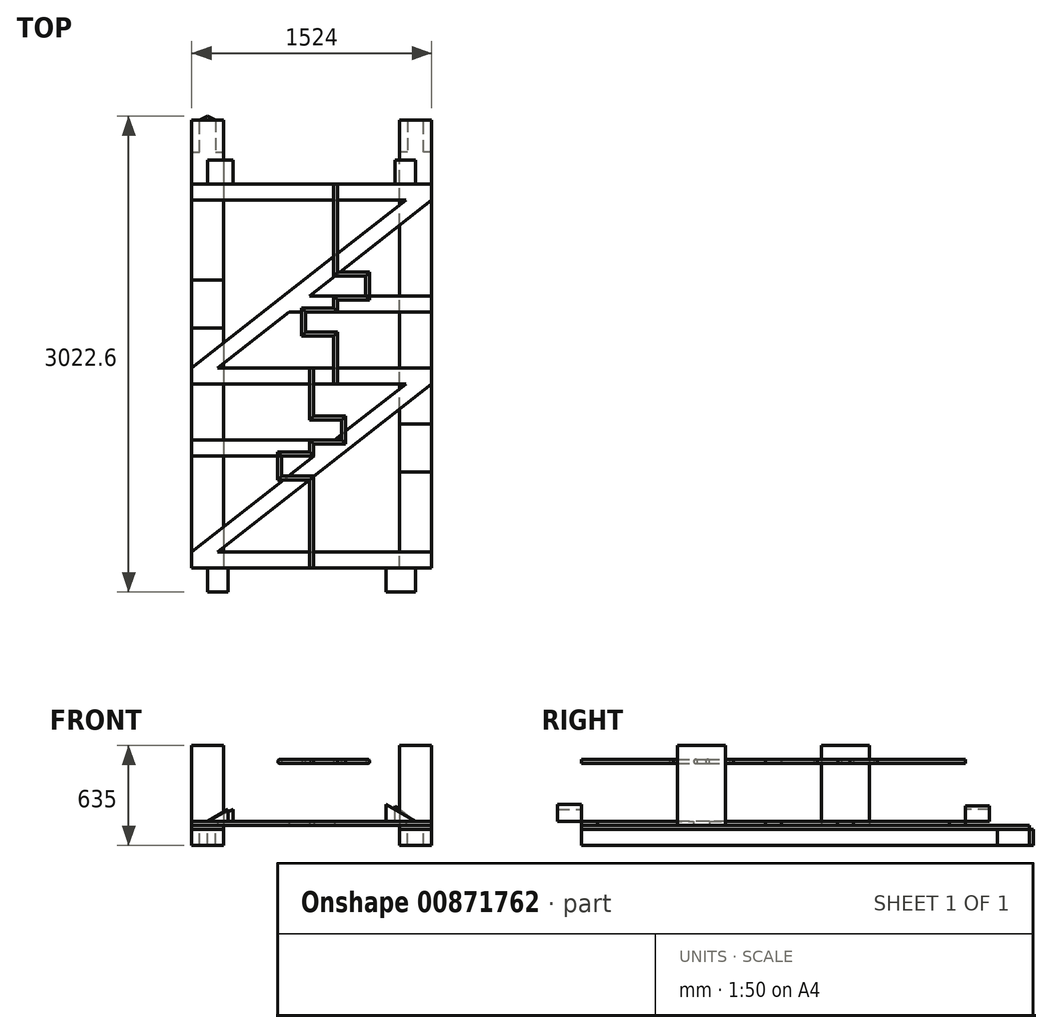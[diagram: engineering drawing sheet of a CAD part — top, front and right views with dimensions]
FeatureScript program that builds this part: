
annotation { "Feature Type Name" : "Feature", "Feature Type Description" : "" }
export const myFeature = defineFeature(function(context is Context, id is Id, definition is map)
    precondition{}
    {
        {
            var Q0;
            Q0=qCreatedBy(makeId("Top.planeOp"),FACE);
            cPlane(context, id + "F0", {"entities" : qUnion([Q0]), "cplaneType" : CPlaneType.OFFSET, "offset" : 406.4 * mm, "width" : 152.4 * mm, "height" : 152.4 * mm});
        }
        {
            var Q0;
            Q0=qCreatedBy(makeId("Top.planeOp"),FACE);
            var sketch = newSketch(context, id + "F1", { "sketchPlane" : qUnion([Q0])});
            skLineSegment(sketch, "E0.bottom", {"start": v(-762, 1219.2) * mm, "end": v(-558.8, 1219.2) * mm});
            skLineSegment(sketch, "E0.top", {"start": v(-762, -1219.2) * mm, "end": v(-558.8, -1219.2) * mm});
            skLineSegment(sketch, "E0.left", {"start": v(-762, 1219.2) * mm, "end": v(-762, -1219.2) * mm});
            skLineSegment(sketch, "E0.right", {"start": v(-558.8, 1219.2) * mm, "end": v(-558.8, -1219.2) * mm});
            skLineSegment(sketch, "E1.bottom", {"start": v(-558.8, -1219.2) * mm, "end": v(558.8, -1219.2) * mm});
            skLineSegment(sketch, "E1.top", {"start": v(-558.8, 1219.2) * mm, "end": v(558.8, 1219.2) * mm});
            skLineSegment(sketch, "E1.right", {"start": v(558.8, -1219.2) * mm, "end": v(558.8, 1219.2) * mm});
            skLineSegment(sketch, "E2.bottom", {"start": v(558.8, -1219.2) * mm, "end": v(762, -1219.2) * mm});
            skLineSegment(sketch, "E2.top", {"start": v(558.8, 1219.2) * mm, "end": v(762, 1219.2) * mm});
            skLineSegment(sketch, "E2.right", {"start": v(762, -1219.2) * mm, "end": v(762, 1219.2) * mm});
            skLineSegment(sketch, "E3", {"start": v(0, 1219.2) * mm, "end": v(0, -1219.2) * mm});
            skLineSegment(sketch, "E4", {"start": v(152.4, 1219.2) * mm, "end": v(152.4, -50.8) * mm});
            skPoint(sketch, "E5", {"position": v(0, 0) * mm});
            skLineSegment(sketch, "E6", {"start": v(152.4, 647.7) * mm, "end": v(355.6, 647.7) * mm});
            skLineSegment(sketch, "E7", {"start": v(355.6, 647.7) * mm, "end": v(355.6, 495.3) * mm});
            skLineSegment(sketch, "E8", {"start": v(355.6, 495.3) * mm, "end": v(152.4, 495.3) * mm});
            skPoint(sketch, "E9", {"position": v(152.4, 457.2) * mm});
            skPoint(sketch, "E10", {"position": v(355.6, 571.5) * mm});
            skLineSegment(sketch, "E11", {"start": v(152.4, 419.1) * mm, "end": v(-50.8, 419.1) * mm});
            skLineSegment(sketch, "E12", {"start": v(-50.8, 419.1) * mm, "end": v(-50.8, 266.7) * mm});
            skLineSegment(sketch, "E13", {"start": v(-50.8, 266.7) * mm, "end": v(152.4, 266.7) * mm});
            skPoint(sketch, "E14", {"position": v(-50.8, 342.9) * mm});
            skLineSegment(sketch, "E15", {"start": v(-762, 609.6) * mm, "end": v(-558.8, 609.6) * mm});
            skLineSegment(sketch, "E16", {"start": v(-762, 304.8) * mm, "end": v(-558.8, 304.8) * mm});
            skPoint(sketch, "E17", {"position": v(-558.8, 457.2) * mm});
            skLineSegment(sketch, "E18", {"start": v(762, -304.8) * mm, "end": v(558.8, -304.8) * mm});
            skLineSegment(sketch, "E19", {"start": v(558.8, -304.8) * mm, "end": v(558.8, -609.6) * mm});
            skLineSegment(sketch, "E20", {"start": v(558.8, -609.6) * mm, "end": v(762, -609.6) * mm});
            skPoint(sketch, "E21", {"position": v(558.8, -457.2) * mm});
            skLineSegment(sketch, "E22", {"start": v(-762, 1219.2) * mm, "end": v(-762, 1422.4) * mm});
            skLineSegment(sketch, "E23", {"start": v(-762, 1422.4) * mm, "end": v(-558.8, 1422.4) * mm});
            skLineSegment(sketch, "E24", {"start": v(-558.8, 1422.4) * mm, "end": v(-558.8, 1219.2) * mm});
            skLineSegment(sketch, "E25", {"start": v(-660.4, 1422.4) * mm, "end": v(-660.4, 1219.2) * mm});
            skLineSegment(sketch, "E26", {"start": v(-711.2, 1422.4) * mm, "end": v(-711.2, 1625.6) * mm});
            skLineSegment(sketch, "E27", {"start": v(-711.2, 1625.6) * mm, "end": v(-609.6, 1625.6) * mm});
            skLineSegment(sketch, "E28", {"start": v(-609.6, 1625.6) * mm, "end": v(-609.6, 1422.4) * mm});
            skLineSegment(sketch, "E29", {"start": v(-711.2, 1625.6) * mm, "end": v(-660.4, 1651) * mm});
            skLineSegment(sketch, "E30", {"start": v(-660.4, 1651) * mm, "end": v(-609.6, 1625.6) * mm});
            skLineSegment(sketch, "E31", {"start": v(-660.4, 1625.6) * mm, "end": v(-660.4, 1651) * mm, "construction": true});
            skLineSegment(sketch, "E32.MirrorCS", {"start": v(711.2, 1625.6) * mm, "end": v(609.6, 1625.6) * mm});
            skLineSegment(sketch, "E33.MirrorCS", {"start": v(660.4, 1625.6) * mm, "end": v(660.4, 1651) * mm, "construction": true});
            skLineSegment(sketch, "E34.MirrorCS", {"start": v(660.4, 1651) * mm, "end": v(609.6, 1625.6) * mm});
            skLineSegment(sketch, "E35.MirrorCS", {"start": v(711.2, 1625.6) * mm, "end": v(660.4, 1651) * mm});
            skLineSegment(sketch, "E36.MirrorCS", {"start": v(762, 1422.4) * mm, "end": v(558.8, 1422.4) * mm});
            skLineSegment(sketch, "E37.MirrorCS", {"start": v(609.6, 1625.6) * mm, "end": v(609.6, 1422.4) * mm});
            skLineSegment(sketch, "E38.MirrorCS", {"start": v(711.2, 1422.4) * mm, "end": v(711.2, 1625.6) * mm});
            skLineSegment(sketch, "E39.MirrorCS", {"start": v(558.8, 1422.4) * mm, "end": v(558.8, 1219.2) * mm});
            skLineSegment(sketch, "E40.MirrorCS", {"start": v(762, 1219.2) * mm, "end": v(762, 1422.4) * mm});
            skLineSegment(sketch, "E41.MirrorCS", {"start": v(660.4, 1422.4) * mm, "end": v(660.4, 1219.2) * mm});
            skLineSegment(sketch, "E42", {"start": v(-762, 1422.4) * mm, "end": v(-762, 1625.6) * mm});
            skLineSegment(sketch, "E43", {"start": v(-762, 1625.6) * mm, "end": v(-558.8, 1625.6) * mm});
            skLineSegment(sketch, "E44", {"start": v(-558.8, 1625.6) * mm, "end": v(-558.8, 1422.4) * mm});
            skLineSegment(sketch, "E45.MirrorCS", {"start": v(558.8, 1625.6) * mm, "end": v(558.8, 1422.4) * mm});
            skLineSegment(sketch, "E46.MirrorCS", {"start": v(762, 1422.4) * mm, "end": v(762, 1625.6) * mm});
            skLineSegment(sketch, "E47.MirrorCS", {"start": v(762, 1625.6) * mm, "end": v(558.8, 1625.6) * mm});
            skLineSegment(sketch, "E48", {"start": v(-660.4, -1219.2) * mm, "end": v(-660.4, 1219.2) * mm, "construction": true});
            skLineSegment(sketch, "E49", {"start": v(660.4, -1219.2) * mm, "end": v(660.4, 1219.2) * mm, "construction": true});
            skSolve(sketch);
        }
        {
            var Q0;
            {var subQ3=sQuery(id+"F1.wireOp",EDGE,"E15");Q0=makeQuery(id+"F1.imprint","IMPRINT",FACE,{"disambiguationData":[TD([[makeQuery(id+"F1.imprint","IMPRINT",EDGE,{"derivedFrom":subQ3}),1.0]])]});}
            var Q1;
            {var subQ0=sQuery(id+"F1.wireOp",EDGE,"E15");Q1=makeQuery(id+"F1.imprint","IMPRINT",FACE,{"disambiguationData":[TD([[makeQuery(id+"F1.imprint","IMPRINT",EDGE,{"derivedFrom":subQ0}),-1.0]])]});}
            var Q2;
            {var subQ0=sQuery(id+"F1.wireOp",EDGE,"E0.top");Q2=makeQuery(id+"F1.imprint","IMPRINT",FACE,{"disambiguationData":[TD([[makeQuery(id+"F1.imprint","IMPRINT",EDGE,{"derivedFrom":subQ0}),1.0]])]});}
            var Q3;
            {var subQ0=sQuery(id+"F1.wireOp",EDGE,"E2.bottom");Q3=makeQuery(id+"F1.imprint","IMPRINT",FACE,{"disambiguationData":[TD([[makeQuery(id+"F1.imprint","IMPRINT",EDGE,{"derivedFrom":subQ0}),1.0]])]});}
            var Q4;
            {var subQ3=sQuery(id+"F1.wireOp",EDGE,"E18");Q4=makeQuery(id+"F1.imprint","IMPRINT",FACE,{"disambiguationData":[TD([[makeQuery(id+"F1.imprint","IMPRINT",EDGE,{"derivedFrom":subQ3}),-1.0]])]});}
            var Q5;
            {var subQ0=sQuery(id+"F1.wireOp",EDGE,"E18");Q5=makeQuery(id+"F1.imprint","IMPRINT",FACE,{"disambiguationData":[TD([[makeQuery(id+"F1.imprint","IMPRINT",EDGE,{"derivedFrom":subQ0}),1.0]])]});}
            var Q6;
            {var subQ1=sQuery(id+"F1.wireOp",EDGE,"E26");Q6=makeQuery(id+"F1.imprint","IMPRINT",FACE,{"disambiguationData":[TD([[makeQuery(id+"F1.imprint","IMPRINT",EDGE,{"derivedFrom":subQ1}),-1.0]])]});}
            var Q7;
            {var subQ0=sQuery(id+"F1.wireOp",EDGE,"E29");Q7=makeQuery(id+"F1.imprint","IMPRINT",FACE,{"disambiguationData":[TD([[makeQuery(id+"F1.imprint","IMPRINT",EDGE,{"derivedFrom":subQ0}),-1.0]])]});}
            var Q8;
            {var subQ0=sQuery(id+"F1.wireOp",EDGE,"E30");Q8=makeQuery(id+"F1.imprint","IMPRINT",FACE,{"disambiguationData":[TD([[makeQuery(id+"F1.imprint","IMPRINT",EDGE,{"derivedFrom":subQ0}),-1.0]])]});}
            var Q9;
            {var subQ0=sQuery(id+"F1.wireOp",EDGE,"E24");Q9=makeQuery(id+"F1.imprint","IMPRINT",FACE,{"disambiguationData":[TD([[makeQuery(id+"F1.imprint","IMPRINT",EDGE,{"derivedFrom":subQ0}),-1.0]])]});}
            var Q10;
            {var subQ3=sQuery(id+"F1.wireOp",EDGE,"E22");Q10=makeQuery(id+"F1.imprint","IMPRINT",FACE,{"disambiguationData":[TD([[makeQuery(id+"F1.imprint","IMPRINT",EDGE,{"derivedFrom":subQ3}),-1.0]])]});}
            var Q11;
            {var subQ0=sQuery(id+"F1.wireOp",EDGE,"E40.MirrorCS");Q11=makeQuery(id+"F1.imprint","IMPRINT",FACE,{"disambiguationData":[TD([[makeQuery(id+"F1.imprint","IMPRINT",EDGE,{"derivedFrom":subQ0}),1.0]])]});}
            var Q12;
            {var subQ0=sQuery(id+"F1.wireOp",EDGE,"E37.MirrorCS");Q12=makeQuery(id+"F1.imprint","IMPRINT",FACE,{"disambiguationData":[TD([[makeQuery(id+"F1.imprint","IMPRINT",EDGE,{"derivedFrom":subQ0}),1.0]])]});}
            var Q13;
            {var subQ0=sQuery(id+"F1.wireOp",EDGE,"E39.MirrorCS");Q13=makeQuery(id+"F1.imprint","IMPRINT",FACE,{"disambiguationData":[TD([[makeQuery(id+"F1.imprint","IMPRINT",EDGE,{"derivedFrom":subQ0}),1.0]])]});}
            var Q14;
            {var subQ2=sQuery(id+"F1.wireOp",EDGE,"E33.MirrorCS");Q14=makeQuery(id+"F1.imprint","IMPRINT",FACE,{"disambiguationData":[TD([[makeQuery(id+"F1.imprint","IMPRINT",EDGE,{"derivedFrom":subQ2}),1.0]])]});}
            var Q15;
            {var subQ2=sQuery(id+"F1.wireOp",EDGE,"E33.MirrorCS");Q15=makeQuery(id+"F1.imprint","IMPRINT",FACE,{"disambiguationData":[TD([[makeQuery(id+"F1.imprint","IMPRINT",EDGE,{"derivedFrom":subQ2}),-1.0]])]});}
            extrude(context, id + "F2", {"entities" : qUnion([Q0, Q1, Q2, Q3, Q4, Q5, Q6, Q7, Q8, Q9, Q10, Q11, Q12, Q13, Q14, Q15]), "oppositeDirection" : true, "depth" : 127 * mm, "offsetDistance" : 25.4 * mm, "hasSecondDirection" : true, "secondDirectionOppositeDirection" : true, "secondDirectionDepth" : 25.4 * mm});
        }
        {
            var Q0;
            {var subQ0=sQuery(id+"F1.wireOp",EDGE,"E15");Q0=makeQuery(id+"F1.imprint","IMPRINT",FACE,{"disambiguationData":[TD([[makeQuery(id+"F1.imprint","IMPRINT",EDGE,{"derivedFrom":subQ0}),-1.0]])]});}
            extrude(context, id + "F3", {"entities" : qUnion([Q0]), "depth" : 508 * mm, "offsetDistance" : 25.4 * mm});
        }
        {
            var Q0;
            {var subQ0=sQuery(id+"F1.wireOp",EDGE,"E18");Q0=makeQuery(id+"F1.imprint","IMPRINT",FACE,{"disambiguationData":[TD([[makeQuery(id+"F1.imprint","IMPRINT",EDGE,{"derivedFrom":subQ0}),1.0]])]});}
            extrude(context, id + "F4", {"entities" : qUnion([Q0]), "depth" : 508 * mm, "offsetDistance" : 25.4 * mm});
        }
        {
            var Q0;
            Q0=qCreatedBy(id+"F0.planeOp",FACE);
            var sketch = newSketch(context, id + "F5", { "sketchPlane" : qUnion([Q0])});
            skLineSegment(sketch, "E50.0", {"start": v(0, 50.8) * mm, "end": v(0, -266.7) * mm});
            skLineSegment(sketch, "E51", {"start": v(0, -266.7) * mm, "end": v(203.2, -266.7) * mm});
            skLineSegment(sketch, "E52", {"start": v(203.2, -266.7) * mm, "end": v(203.2, -419.1) * mm});
            skLineSegment(sketch, "E53", {"start": v(203.2, -419.1) * mm, "end": v(0, -419.1) * mm});
            skLineSegment(sketch, "E54", {"start": v(0, -495.3) * mm, "end": v(-203.2, -495.3) * mm});
            skLineSegment(sketch, "E55", {"start": v(-203.2, -495.3) * mm, "end": v(-203.2, -647.7) * mm});
            skLineSegment(sketch, "E56", {"start": v(-203.2, -647.7) * mm, "end": v(0, -647.7) * mm});
            skPoint(sketch, "E57", {"position": v(0, -457.2) * mm});
            skPoint(sketch, "E58", {"position": v(203.2, -342.9) * mm});
            skPoint(sketch, "E59", {"position": v(-203.2, -571.5) * mm});
            skPoint(sketch, "E60.orphan", {"position": v(0, 1219.2) * mm});
            skLineSegment(sketch, "E61.0", {"start": v(152.4, 1219.2) * mm, "end": v(152.4, 647.7) * mm});
            skLineSegment(sketch, "E61.1", {"start": v(152.4, 647.7) * mm, "end": v(355.6, 647.7) * mm});
            skLineSegment(sketch, "E61.2", {"start": v(355.6, 495.3) * mm, "end": v(152.4, 495.3) * mm});
            skLineSegment(sketch, "E61.3", {"start": v(355.6, 647.7) * mm, "end": v(355.6, 495.3) * mm});
            skLineSegment(sketch, "E61.4", {"start": v(152.4, 419.1) * mm, "end": v(-50.8, 419.1) * mm});
            skLineSegment(sketch, "E61.5", {"start": v(-50.8, 419.1) * mm, "end": v(-50.8, 266.7) * mm});
            skLineSegment(sketch, "E61.6", {"start": v(-50.8, 266.7) * mm, "end": v(152.4, 266.7) * mm});
            skLineSegment(sketch, "E62.trimOffspring", {"start": v(152.4, 495.3) * mm, "end": v(152.4, 419.1) * mm});
            skLineSegment(sketch, "E63.trimOffspring", {"start": v(152.4, 266.7) * mm, "end": v(152.4, -50.8) * mm});
            skLineSegment(sketch, "E64.trimOffspring", {"start": v(0, -419.1) * mm, "end": v(0, -495.3) * mm});
            skLineSegment(sketch, "E65.trimOffspring", {"start": v(0, -647.7) * mm, "end": v(0, -1219.2) * mm});
            skSolve(sketch);
        }
        {
            var Q0;
            {var subQ2=sQuery(id+"F1.wireOp",EDGE,"E26");Q0=makeQuery(id+"F1.imprint","IMPRINT",FACE,{"disambiguationData":[TD([[makeQuery(id+"F1.imprint","IMPRINT",EDGE,{"derivedFrom":subQ2}),1.0]])]});}
            var Q1;
            {var subQ3=sQuery(id+"F1.wireOp",EDGE,"E26");Q1=makeQuery(id+"F1.imprint","IMPRINT",FACE,{"disambiguationData":[TD([[makeQuery(id+"F1.imprint","IMPRINT",EDGE,{"derivedFrom":subQ3}),-1.0]])]});}
            var Q2;
            {var subQ2=sQuery(id+"F1.wireOp",EDGE,"E28");Q2=makeQuery(id+"F1.imprint","IMPRINT",FACE,{"disambiguationData":[TD([[makeQuery(id+"F1.imprint","IMPRINT",EDGE,{"derivedFrom":subQ2}),1.0]])]});}
            var Q3;
            {var subQ0=sQuery(id+"F1.wireOp",EDGE,"E24");Q3=makeQuery(id+"F1.imprint","IMPRINT",FACE,{"disambiguationData":[TD([[makeQuery(id+"F1.imprint","IMPRINT",EDGE,{"derivedFrom":subQ0}),-1.0]])]});}
            var Q4;
            {var subQ3=sQuery(id+"F1.wireOp",EDGE,"E22");Q4=makeQuery(id+"F1.imprint","IMPRINT",FACE,{"disambiguationData":[TD([[makeQuery(id+"F1.imprint","IMPRINT",EDGE,{"derivedFrom":subQ3}),-1.0]])]});}
            var Q5;
            {var subQ3=sQuery(id+"F1.wireOp",EDGE,"E15");Q5=makeQuery(id+"F1.imprint","IMPRINT",FACE,{"disambiguationData":[TD([[makeQuery(id+"F1.imprint","IMPRINT",EDGE,{"derivedFrom":subQ3}),1.0]])]});}
            var Q6;
            {var subQ0=sQuery(id+"F1.wireOp",EDGE,"E0.top");Q6=makeQuery(id+"F1.imprint","IMPRINT",FACE,{"disambiguationData":[TD([[makeQuery(id+"F1.imprint","IMPRINT",EDGE,{"derivedFrom":subQ0}),1.0]])]});}
            var Q7;
            {var subQ3=sQuery(id+"F1.wireOp",EDGE,"E18");Q7=makeQuery(id+"F1.imprint","IMPRINT",FACE,{"disambiguationData":[TD([[makeQuery(id+"F1.imprint","IMPRINT",EDGE,{"derivedFrom":subQ3}),-1.0]])]});}
            var Q8;
            {var subQ0=sQuery(id+"F1.wireOp",EDGE,"E2.bottom");Q8=makeQuery(id+"F1.imprint","IMPRINT",FACE,{"disambiguationData":[TD([[makeQuery(id+"F1.imprint","IMPRINT",EDGE,{"derivedFrom":subQ0}),1.0]])]});}
            var Q9;
            {var subQ2=sQuery(id+"F1.wireOp",EDGE,"E37.MirrorCS");Q9=makeQuery(id+"F1.imprint","IMPRINT",FACE,{"disambiguationData":[TD([[makeQuery(id+"F1.imprint","IMPRINT",EDGE,{"derivedFrom":subQ2}),-1.0]])]});}
            var Q10;
            {var subQ1=sQuery(id+"F1.wireOp",EDGE,"E37.MirrorCS");Q10=makeQuery(id+"F1.imprint","IMPRINT",FACE,{"disambiguationData":[TD([[makeQuery(id+"F1.imprint","IMPRINT",EDGE,{"derivedFrom":subQ1}),1.0]])]});}
            var Q11;
            {var subQ2=sQuery(id+"F1.wireOp",EDGE,"E38.MirrorCS");Q11=makeQuery(id+"F1.imprint","IMPRINT",FACE,{"disambiguationData":[TD([[makeQuery(id+"F1.imprint","IMPRINT",EDGE,{"derivedFrom":subQ2}),-1.0]])]});}
            var Q12;
            {var subQ0=sQuery(id+"F1.wireOp",EDGE,"E40.MirrorCS");Q12=makeQuery(id+"F1.imprint","IMPRINT",FACE,{"disambiguationData":[TD([[makeQuery(id+"F1.imprint","IMPRINT",EDGE,{"derivedFrom":subQ0}),1.0]])]});}
            var Q13;
            {var subQ0=sQuery(id+"F1.wireOp",EDGE,"E39.MirrorCS");Q13=makeQuery(id+"F1.imprint","IMPRINT",FACE,{"disambiguationData":[TD([[makeQuery(id+"F1.imprint","IMPRINT",EDGE,{"derivedFrom":subQ0}),1.0]])]});}
            var Q14;
            {var subQ0=sQuery(id+"F1.wireOp",EDGE,"E15");Q14=makeQuery(id+"F1.imprint","IMPRINT",FACE,{"disambiguationData":[TD([[makeQuery(id+"F1.imprint","IMPRINT",EDGE,{"derivedFrom":subQ0}),-1.0]])]});}
            var Q15;
            {var subQ0=sQuery(id+"F1.wireOp",EDGE,"E18");Q15=makeQuery(id+"F1.imprint","IMPRINT",FACE,{"disambiguationData":[TD([[makeQuery(id+"F1.imprint","IMPRINT",EDGE,{"derivedFrom":subQ0}),1.0]])]});}
            extrude(context, id + "F6", {"entities" : qUnion([Q0, Q1, Q2, Q3, Q4, Q5, Q6, Q7, Q8, Q9, Q10, Q11, Q12, Q13, Q14, Q15]), "oppositeDirection" : true, "depth" : 25.4 * mm, "offsetDistance" : 25.4 * mm});
        }
        {
            var Q0;
            Q0=qCreatedBy(makeId("Top.planeOp"),FACE);
            var sketch = newSketch(context, id + "F7", { "sketchPlane" : qUnion([Q0])});
            skLineSegment(sketch, "E66.0", {"start": v(-762, 1219.2) * mm, "end": v(-762, -1219.2) * mm});
            skLineSegment(sketch, "E66.1", {"start": v(-558.8, 1219.2) * mm, "end": v(-558.8, -1219.2) * mm});
            skLineSegment(sketch, "E66.2", {"start": v(558.8, -1219.2) * mm, "end": v(558.8, 1219.2) * mm});
            skLineSegment(sketch, "E66.3", {"start": v(762, -1219.2) * mm, "end": v(762, 1219.2) * mm});
            skLineSegment(sketch, "E67.0", {"start": v(-558.8, 1219.2) * mm, "end": v(558.8, 1219.2) * mm});
            skLineSegment(sketch, "E67.1", {"start": v(-762, 1219.2) * mm, "end": v(-558.8, 1219.2) * mm});
            skLineSegment(sketch, "E67.2", {"start": v(558.8, 1219.2) * mm, "end": v(762, 1219.2) * mm});
            skLineSegment(sketch, "E67.3", {"start": v(0, 1219.2) * mm, "end": v(0, -1219.2) * mm});
            skLineSegment(sketch, "E67.4", {"start": v(-558.8, -1219.2) * mm, "end": v(558.8, -1219.2) * mm});
            skLineSegment(sketch, "E67.5", {"start": v(-762, -1219.2) * mm, "end": v(-558.8, -1219.2) * mm});
            skLineSegment(sketch, "E67.6", {"start": v(558.8, -1219.2) * mm, "end": v(762, -1219.2) * mm});
            skLineSegment(sketch, "E68", {"start": v(-762, 1117.6) * mm, "end": v(762, 1117.6) * mm});
            skLineSegment(sketch, "E69", {"start": v(-762, -1117.6) * mm, "end": v(762, -1117.6) * mm});
            skLineSegment(sketch, "E70", {"start": v(-762, 0) * mm, "end": v(762, 0) * mm, "construction": true});
            skLineSegment(sketch, "E71", {"start": v(-762, 50.8) * mm, "end": v(762, 50.8) * mm});
            skLineSegment(sketch, "E72.MirrorCS", {"start": v(-762, -50.8) * mm, "end": v(762, -50.8) * mm});
            skLineSegment(sketch, "E73", {"start": v(-762, -1117.6) * mm, "end": v(597.43, -50.8) * mm});
            skLineSegment(sketch, "E74", {"start": v(762, -50.8) * mm, "end": v(-597.43, -1117.6) * mm});
            skLineSegment(sketch, "E75", {"start": v(597.43, 1117.6) * mm, "end": v(-762, 50.8) * mm});
            skLineSegment(sketch, "E76", {"start": v(-597.43, 50.8) * mm, "end": v(762, 1117.6) * mm});
            skLineSegment(sketch, "E77", {"start": v(-14.81, 508) * mm, "end": v(762, 508) * mm});
            skLineSegment(sketch, "E78", {"start": v(762, 406.4) * mm, "end": v(-144.28, 406.4) * mm});
            skLineSegment(sketch, "E79", {"start": v(762, 457.2) * mm, "end": v(-79.55, 457.2) * mm, "construction": true});
            skLineSegment(sketch, "E80", {"start": v(-762, -406.4) * mm, "end": v(144.28, -406.4) * mm});
            skLineSegment(sketch, "E81", {"start": v(14.81, -508) * mm, "end": v(-762, -508) * mm});
            skLineSegment(sketch, "E82", {"start": v(-762, -457.2) * mm, "end": v(79.55, -457.2) * mm, "construction": true});
            skSolve(sketch);
        }
        {
            var Q0;
            {var subQ0=sQuery(id+"F7.wireOp",EDGE,"E75");var subQ1=sQuery(id+"F7.wireOp",EDGE,"E66.1");var subQ2=makeQuery(id+"F7.imprint","INTERSECT",VERTEX,{"derivedFrom":[subQ1,subQ0]});Q0=makeQuery(id+"F7.imprint","IMPRINT",FACE,{"disambiguationData":[TD([[makeQuery(id+"F7.imprint","IMPRINT",EDGE,{"disambiguationData":[TD([[subQ2,-1.0]])],"derivedFrom":subQ1}),1.0]])]});}
            var Q1;
            {var subQ0=sQuery(id+"F7.wireOp",EDGE,"E75");var subQ1=sQuery(id+"F7.wireOp",EDGE,"E66.1");var subQ2=makeQuery(id+"F7.imprint","INTERSECT",VERTEX,{"derivedFrom":[subQ1,subQ0]});Q1=makeQuery(id+"F7.imprint","IMPRINT",FACE,{"disambiguationData":[TD([[makeQuery(id+"F7.imprint","IMPRINT",EDGE,{"disambiguationData":[TD([[subQ2,-1.0]])],"derivedFrom":subQ1}),-1.0]])]});}
            var Q2;
            {var subQ0=sQuery(id+"F7.wireOp",EDGE,"E76");var subQ1=sQuery(id+"F7.wireOp",EDGE,"E66.2");var subQ2=makeQuery(id+"F7.imprint","INTERSECT",VERTEX,{"derivedFrom":[subQ1,subQ0]});Q2=makeQuery(id+"F7.imprint","IMPRINT",FACE,{"disambiguationData":[TD([[makeQuery(id+"F7.imprint","IMPRINT",EDGE,{"disambiguationData":[TD([[subQ2,-1.0]])],"derivedFrom":subQ1}),1.0]])]});}
            var Q3;
            {var subQ0=sQuery(id+"F7.wireOp",EDGE,"E76");var subQ1=sQuery(id+"F7.wireOp",EDGE,"E66.2");var subQ2=makeQuery(id+"F7.imprint","INTERSECT",VERTEX,{"derivedFrom":[subQ1,subQ0]});Q3=makeQuery(id+"F7.imprint","IMPRINT",FACE,{"disambiguationData":[TD([[makeQuery(id+"F7.imprint","IMPRINT",EDGE,{"disambiguationData":[TD([[subQ2,-1.0]])],"derivedFrom":subQ1}),-1.0]])]});}
            var Q4;
            {var subQ4=sQuery(id+"F7.wireOp",EDGE,"E67.2");Q4=makeQuery(id+"F7.imprint","IMPRINT",FACE,{"disambiguationData":[TD([[makeQuery(id+"F7.imprint","IMPRINT",EDGE,{"derivedFrom":subQ4}),-1.0]])]});}
            var Q5;
            {var subQ0=sQuery(id+"F7.wireOp",EDGE,"E67.0");var subQ5=sQuery(id+"F7.wireOp",EDGE,"E67.3");var subQ6=makeQuery(id+"F7.imprint","INTERSECT",VERTEX,{"derivedFrom":[subQ0,subQ5]});Q5=makeQuery(id+"F7.imprint","IMPRINT",FACE,{"disambiguationData":[TD([[makeQuery(id+"F7.imprint","IMPRINT",EDGE,{"disambiguationData":[TD([[subQ6,-1.0]])],"derivedFrom":subQ5}),1.0]])]});}
            var Q6;
            {var subQ0=sQuery(id+"F7.wireOp",EDGE,"E67.0");var subQ5=sQuery(id+"F7.wireOp",EDGE,"E67.3");var subQ6=makeQuery(id+"F7.imprint","INTERSECT",VERTEX,{"derivedFrom":[subQ0,subQ5]});Q6=makeQuery(id+"F7.imprint","IMPRINT",FACE,{"disambiguationData":[TD([[makeQuery(id+"F7.imprint","IMPRINT",EDGE,{"disambiguationData":[TD([[subQ6,-1.0]])],"derivedFrom":subQ5}),-1.0]])]});}
            var Q7;
            {var subQ0=sQuery(id+"F7.wireOp",EDGE,"E67.1");Q7=makeQuery(id+"F7.imprint","IMPRINT",FACE,{"disambiguationData":[TD([[makeQuery(id+"F7.imprint","IMPRINT",EDGE,{"derivedFrom":subQ0}),-1.0]])]});}
            var Q8;
            {var subQ0=sQuery(id+"F7.wireOp",EDGE,"E71");var subQ1=sQuery(id+"F7.wireOp",EDGE,"E66.1");var subQ2=makeQuery(id+"F7.imprint","INTERSECT",VERTEX,{"derivedFrom":[subQ1,subQ0]});Q8=makeQuery(id+"F7.imprint","IMPRINT",FACE,{"disambiguationData":[TD([[makeQuery(id+"F7.imprint","IMPRINT",EDGE,{"disambiguationData":[TD([[subQ2,-1.0]])],"derivedFrom":subQ1}),1.0]])]});}
            var Q9;
            {var subQ0=sQuery(id+"F7.wireOp",EDGE,"E71");var subQ2=sQuery(id+"F7.wireOp",EDGE,"E66.1");var subQ3=makeQuery(id+"F7.imprint","INTERSECT",VERTEX,{"derivedFrom":[subQ2,subQ0]});Q9=makeQuery(id+"F7.imprint","IMPRINT",FACE,{"disambiguationData":[TD([[makeQuery(id+"F7.imprint","IMPRINT",EDGE,{"disambiguationData":[TD([[subQ3,-1.0]])],"derivedFrom":subQ2}),-1.0]])]});}
            var Q10;
            {var subQ0=sQuery(id+"F7.wireOp",EDGE,"E72.MirrorCS");var subQ1=sQuery(id+"F7.wireOp",EDGE,"E66.2");var subQ2=makeQuery(id+"F7.imprint","INTERSECT",VERTEX,{"derivedFrom":[subQ1,subQ0]});Q10=makeQuery(id+"F7.imprint","IMPRINT",FACE,{"disambiguationData":[TD([[makeQuery(id+"F7.imprint","IMPRINT",EDGE,{"disambiguationData":[TD([[subQ2,-1.0]])],"derivedFrom":subQ1}),1.0]])]});}
            var Q11;
            {var subQ3=sQuery(id+"F7.wireOp",EDGE,"E66.2");var subQ5=sQuery(id+"F7.wireOp",EDGE,"E72.MirrorCS");var subQ8=makeQuery(id+"F7.imprint","INTERSECT",VERTEX,{"derivedFrom":[subQ3,subQ5]});Q11=makeQuery(id+"F7.imprint","IMPRINT",FACE,{"disambiguationData":[TD([[makeQuery(id+"F7.imprint","IMPRINT",EDGE,{"disambiguationData":[TD([[subQ8,-1.0]])],"derivedFrom":subQ3}),-1.0]])]});}
            var Q12;
            {var subQ0=sQuery(id+"F7.wireOp",EDGE,"E74");var subQ1=sQuery(id+"F7.wireOp",EDGE,"E66.2");var subQ2=makeQuery(id+"F7.imprint","INTERSECT",VERTEX,{"derivedFrom":[subQ1,subQ0]});Q12=makeQuery(id+"F7.imprint","IMPRINT",FACE,{"disambiguationData":[TD([[makeQuery(id+"F7.imprint","IMPRINT",EDGE,{"disambiguationData":[TD([[subQ2,-1.0]])],"derivedFrom":subQ1}),1.0]])]});}
            var Q13;
            {var subQ0=sQuery(id+"F7.wireOp",EDGE,"E74");var subQ1=sQuery(id+"F7.wireOp",EDGE,"E66.2");var subQ2=makeQuery(id+"F7.imprint","INTERSECT",VERTEX,{"derivedFrom":[subQ1,subQ0]});Q13=makeQuery(id+"F7.imprint","IMPRINT",FACE,{"disambiguationData":[TD([[makeQuery(id+"F7.imprint","IMPRINT",EDGE,{"disambiguationData":[TD([[subQ2,-1.0]])],"derivedFrom":subQ1}),-1.0]])]});}
            var Q14;
            {var subQ0=sQuery(id+"F7.wireOp",EDGE,"E73");var subQ1=sQuery(id+"F7.wireOp",EDGE,"E66.1");var subQ2=makeQuery(id+"F7.imprint","INTERSECT",VERTEX,{"derivedFrom":[subQ1,subQ0]});Q14=makeQuery(id+"F7.imprint","IMPRINT",FACE,{"disambiguationData":[TD([[makeQuery(id+"F7.imprint","IMPRINT",EDGE,{"disambiguationData":[TD([[subQ2,-1.0]])],"derivedFrom":subQ1}),1.0]])]});}
            var Q15;
            {var subQ0=sQuery(id+"F7.wireOp",EDGE,"E73");var subQ1=sQuery(id+"F7.wireOp",EDGE,"E66.1");var subQ2=makeQuery(id+"F7.imprint","INTERSECT",VERTEX,{"derivedFrom":[subQ1,subQ0]});Q15=makeQuery(id+"F7.imprint","IMPRINT",FACE,{"disambiguationData":[TD([[makeQuery(id+"F7.imprint","IMPRINT",EDGE,{"disambiguationData":[TD([[subQ2,-1.0]])],"derivedFrom":subQ1}),-1.0]])]});}
            var Q16;
            {var subQ0=sQuery(id+"F7.wireOp",EDGE,"E67.4");var subQ5=sQuery(id+"F7.wireOp",EDGE,"E67.3");var subQ6=makeQuery(id+"F7.imprint","INTERSECT",VERTEX,{"derivedFrom":[subQ5,subQ0]});Q16=makeQuery(id+"F7.imprint","IMPRINT",FACE,{"disambiguationData":[TD([[makeQuery(id+"F7.imprint","IMPRINT",EDGE,{"disambiguationData":[TD([[subQ6,1.0]])],"derivedFrom":subQ5}),-1.0]])]});}
            var Q17;
            {var subQ4=sQuery(id+"F7.wireOp",EDGE,"E67.5");Q17=makeQuery(id+"F7.imprint","IMPRINT",FACE,{"disambiguationData":[TD([[makeQuery(id+"F7.imprint","IMPRINT",EDGE,{"derivedFrom":subQ4}),1.0]])]});}
            var Q18;
            {var subQ0=sQuery(id+"F7.wireOp",EDGE,"E67.4");var subQ5=sQuery(id+"F7.wireOp",EDGE,"E67.3");var subQ6=makeQuery(id+"F7.imprint","INTERSECT",VERTEX,{"derivedFrom":[subQ5,subQ0]});Q18=makeQuery(id+"F7.imprint","IMPRINT",FACE,{"disambiguationData":[TD([[makeQuery(id+"F7.imprint","IMPRINT",EDGE,{"disambiguationData":[TD([[subQ6,1.0]])],"derivedFrom":subQ5}),1.0]])]});}
            var Q19;
            {var subQ0=sQuery(id+"F7.wireOp",EDGE,"E67.6");Q19=makeQuery(id+"F7.imprint","IMPRINT",FACE,{"disambiguationData":[TD([[makeQuery(id+"F7.imprint","IMPRINT",EDGE,{"derivedFrom":subQ0}),1.0]])]});}
            var Q20;
            {var subQ0=sQuery(id+"F7.wireOp",EDGE,"E80");var subQ1=sQuery(id+"F7.wireOp",EDGE,"E66.1");var subQ2=makeQuery(id+"F7.imprint","INTERSECT",VERTEX,{"derivedFrom":[subQ1,subQ0]});Q20=makeQuery(id+"F7.imprint","IMPRINT",FACE,{"disambiguationData":[TD([[makeQuery(id+"F7.imprint","IMPRINT",EDGE,{"disambiguationData":[TD([[subQ2,-1.0]])],"derivedFrom":subQ1}),1.0]])]});}
            var Q21;
            {var subQ0=sQuery(id+"F7.wireOp",EDGE,"E80");var subQ1=sQuery(id+"F7.wireOp",EDGE,"E66.0");var subQ2=makeQuery(id+"F7.imprint","INTERSECT",VERTEX,{"derivedFrom":[subQ1,subQ0]});Q21=makeQuery(id+"F7.imprint","IMPRINT",FACE,{"disambiguationData":[TD([[makeQuery(id+"F7.imprint","IMPRINT",EDGE,{"disambiguationData":[TD([[subQ2,-1.0]])],"derivedFrom":subQ1}),1.0]])]});}
            var Q22;
            {var subQ0=sQuery(id+"F7.wireOp",EDGE,"E80");var subQ1=sQuery(id+"F7.wireOp",EDGE,"E67.3");var subQ2=makeQuery(id+"F7.imprint","INTERSECT",VERTEX,{"derivedFrom":[subQ1,subQ0]});Q22=makeQuery(id+"F7.imprint","IMPRINT",FACE,{"disambiguationData":[TD([[makeQuery(id+"F7.imprint","IMPRINT",EDGE,{"disambiguationData":[TD([[subQ2,-1.0]])],"derivedFrom":subQ1}),1.0]])]});}
            var Q23;
            {var subQ0=sQuery(id+"F7.wireOp",EDGE,"E77");var subQ1=sQuery(id+"F7.wireOp",EDGE,"E67.3");var subQ2=makeQuery(id+"F7.imprint","INTERSECT",VERTEX,{"derivedFrom":[subQ1,subQ0]});Q23=makeQuery(id+"F7.imprint","IMPRINT",FACE,{"disambiguationData":[TD([[makeQuery(id+"F7.imprint","IMPRINT",EDGE,{"disambiguationData":[TD([[subQ2,-1.0]])],"derivedFrom":subQ1}),-1.0]])]});}
            var Q24;
            {var subQ0=sQuery(id+"F7.wireOp",EDGE,"E78");var subQ1=sQuery(id+"F7.wireOp",EDGE,"E66.2");var subQ2=makeQuery(id+"F7.imprint","INTERSECT",VERTEX,{"derivedFrom":[subQ1,subQ0]});Q24=makeQuery(id+"F7.imprint","IMPRINT",FACE,{"disambiguationData":[TD([[makeQuery(id+"F7.imprint","IMPRINT",EDGE,{"disambiguationData":[TD([[subQ2,-1.0]])],"derivedFrom":subQ1}),-1.0]])]});}
            var Q25;
            {var subQ0=sQuery(id+"F7.wireOp",EDGE,"E78");var subQ1=sQuery(id+"F7.wireOp",EDGE,"E66.2");var subQ2=makeQuery(id+"F7.imprint","INTERSECT",VERTEX,{"derivedFrom":[subQ1,subQ0]});Q25=makeQuery(id+"F7.imprint","IMPRINT",FACE,{"disambiguationData":[TD([[makeQuery(id+"F7.imprint","IMPRINT",EDGE,{"disambiguationData":[TD([[subQ2,-1.0]])],"derivedFrom":subQ1}),1.0]])]});}
            extrude(context, id + "F8", {"entities" : qUnion([Q0, Q1, Q2, Q3, Q4, Q5, Q6, Q7, Q8, Q9, Q10, Q11, Q12, Q13, Q14, Q15, Q16, Q17, Q18, Q19, Q20, Q21, Q22, Q23, Q24, Q25]), "depth" : 25.4 * mm, "offsetDistance" : 25.4 * mm});
        }
        {
            var Q0;
            Q0=makeQuery(id+"F8.opExtrude","SWEPT_FACE",FACE,{"disambiguationData":[OSD([sQuery(id+"F7.wireOp",EDGE,"E67.4"),sQuery(id+"F7.wireOp",EDGE,"E67.5"),sQuery(id+"F7.wireOp",EDGE,"E67.6")])]});
            cPlane(context, id + "F9", {"entities" : qUnion([Q0]), "cplaneType" : CPlaneType.OFFSET, "offset" : 0 * mm, "width" : 152.4 * mm, "height" : 152.4 * mm});
        }
        {
            var Q0;
            Q0=makeQuery(id+"F8.opExtrude","SWEPT_FACE",FACE,{"disambiguationData":[OSD([sQuery(id+"F7.wireOp",EDGE,"E67.0"),sQuery(id+"F7.wireOp",EDGE,"E67.1"),sQuery(id+"F7.wireOp",EDGE,"E67.2")])]});
            cPlane(context, id + "F10", {"entities" : qUnion([Q0]), "cplaneType" : CPlaneType.OFFSET, "offset" : 0 * mm, "width" : 152.4 * mm, "height" : 152.4 * mm});
        }
        {
            var Q0;
            Q0=qCreatedBy(id+"F10.planeOp",FACE);
            var sketch = newSketch(context, id + "F11", { "sketchPlane" : qUnion([Q0])});
            skPoint(sketch, "E83.0", {"position": v(-152.4, 406.4) * mm});
            skCircle(sketch, "E84", {"center": v(-152.4, 406.4) * mm, "radius": 12.7 * mm});
            skPoint(sketch, "E85.0", {"position": v(-762, 25.4) * mm});
            skPoint(sketch, "E85.1", {"position": v(762, 25.4) * mm});
            skPoint(sketch, "E86.0", {"position": v(0, 406.4) * mm});
            skLineSegment(sketch, "E87", {"start": v(-762, 25.4) * mm, "end": v(-660.4, 25.4) * mm, "construction": true});
            skLineSegment(sketch, "E88", {"start": v(762, 25.4) * mm, "end": v(660.4, 25.4) * mm, "construction": true});
            skLineSegment(sketch, "E89", {"start": v(-660.4, 25.4) * mm, "end": v(-529.2, 25.4) * mm});
            skLineSegment(sketch, "E90", {"start": v(-529.2, 25.4) * mm, "end": v(-529.2, 123.8) * mm});
            skLineSegment(sketch, "E91", {"start": v(-529.2, 123.8) * mm, "end": v(-660.4, 25.4) * mm});
            skLineSegment(sketch, "E92", {"start": v(660.4, 25.4) * mm, "end": v(498.96, 25.4) * mm});
            skLineSegment(sketch, "E93", {"start": v(498.96, 25.4) * mm, "end": v(498.96, 101.08) * mm});
            skLineSegment(sketch, "E94", {"start": v(498.96, 101.08) * mm, "end": v(660.4, 25.4) * mm});
            skSolve(sketch);
        }
        {
            var Q0;
            Q0=makeQuery(id+"F11.imprint","IMPRINT",FACE,{"disambiguationData":[TD([[makeQuery(id+"F11.imprint","IMPRINT",EDGE,{"derivedFrom":sQuery(id+"F11.wireOp",EDGE,"E84")}),1.0]])]});
            var Q1;
            Q1=sQuery(id+"F5.wireOp",EDGE,"E61.0");
            var Q2;
            Q2=sQuery(id+"F5.wireOp",EDGE,"E61.1");
            var Q3;
            Q3=sQuery(id+"F5.wireOp",EDGE,"E61.3");
            var Q4;
            Q4=sQuery(id+"F5.wireOp",EDGE,"E61.2");
            var Q5;
            Q5=sQuery(id+"F5.wireOp",EDGE,"E62.trimOffspring");
            var Q6;
            Q6=sQuery(id+"F5.wireOp",EDGE,"E61.4");
            var Q7;
            Q7=sQuery(id+"F5.wireOp",EDGE,"E61.5");
            var Q8;
            Q8=sQuery(id+"F5.wireOp",EDGE,"E63.trimOffspring");
            var Q9;
            Q9=sQuery(id+"F5.wireOp",EDGE,"E61.6");
            sweep(context, id + "F12", {"profiles" : qUnion([Q0]), "path" : qUnion([Q1, Q2, Q3, Q4, Q5, Q6, Q7, Q8, Q9])});
        }
        {
            var Q0;
            Q0=qCreatedBy(id+"F9.planeOp",FACE);
            var sketch = newSketch(context, id + "F13", { "sketchPlane" : qUnion([Q0])});
            skPoint(sketch, "E95.0", {"position": v(0, 406.4) * mm});
            skCircle(sketch, "E96", {"center": v(0, 406.4) * mm, "radius": 12.7 * mm});
            skPoint(sketch, "E97.0", {"position": v(-762, 25.4) * mm});
            skLineSegment(sketch, "E98", {"start": v(-762, 25.4) * mm, "end": v(-660.4, 25.4) * mm, "construction": true});
            skPoint(sketch, "E99.0", {"position": v(762, 25.4) * mm});
            skLineSegment(sketch, "E100", {"start": v(762, 25.4) * mm, "end": v(660.4, 25.4) * mm, "construction": true});
            skPoint(sketch, "E101.0", {"position": v(152.4, 406.4) * mm});
            skLineSegment(sketch, "E102", {"start": v(-530.33, 100.44) * mm, "end": v(-530.33, 27.93) * mm});
            skLineSegment(sketch, "E103", {"start": v(-530.33, 100.44) * mm, "end": v(-660.4, 25.4) * mm});
            skLineSegment(sketch, "E104", {"start": v(470.23, 135.11) * mm, "end": v(470.23, 25.4) * mm});
            skLineSegment(sketch, "E105", {"start": v(470.23, 25.4) * mm, "end": v(660.4, 25.4) * mm});
            skLineSegment(sketch, "E106", {"start": v(470.23, 135.11) * mm, "end": v(660.4, 25.4) * mm});
            skLineSegment(sketch, "E107", {"start": v(-660.4, 25.4) * mm, "end": v(-530.33, 27.93) * mm});
            skSolve(sketch);
        }
        {
            var Q0;
            Q0=makeQuery(id+"F13.imprint","IMPRINT",FACE,{"disambiguationData":[TD([[makeQuery(id+"F13.imprint","IMPRINT",EDGE,{"derivedFrom":sQuery(id+"F13.wireOp",EDGE,"E96")}),1.0]])]});
            var Q1;
            Q1=sQuery(id+"F5.wireOp",EDGE,"E65.trimOffspring");
            var Q2;
            Q2=sQuery(id+"F5.wireOp",EDGE,"E50.0");
            var Q3;
            Q3=sQuery(id+"F5.wireOp",EDGE,"E51");
            var Q4;
            Q4=sQuery(id+"F5.wireOp",EDGE,"E52");
            var Q5;
            Q5=sQuery(id+"F5.wireOp",EDGE,"E53");
            var Q6;
            Q6=sQuery(id+"F5.wireOp",EDGE,"E64.trimOffspring");
            var Q7;
            Q7=sQuery(id+"F5.wireOp",EDGE,"E54");
            var Q8;
            Q8=sQuery(id+"F5.wireOp",EDGE,"E55");
            var Q9;
            Q9=sQuery(id+"F5.wireOp",EDGE,"E56");
            sweep(context, id + "F14", {"profiles" : qUnion([Q0]), "path" : qUnion([Q1, Q2, Q3, Q4, Q5, Q6, Q7, Q8, Q9])});
        }
        {
            var Q0;
            Q0=makeQuery(id+"F13.imprint","IMPRINT",FACE,{"disambiguationData":[TD([[makeQuery(id+"F13.imprint","IMPRINT",EDGE,{"derivedFrom":sQuery(id+"F13.wireOp",EDGE,"E102")}),-1.0]])]});
            var Q1;
            Q1=makeQuery(id+"F13.imprint","IMPRINT",FACE,{"disambiguationData":[TD([[makeQuery(id+"F13.imprint","IMPRINT",EDGE,{"derivedFrom":sQuery(id+"F13.wireOp",EDGE,"E104")}),1.0]])]});
            extrude(context, id + "F15", {"entities" : qUnion([Q0, Q1]), "depth" : 152.4 * mm, "offsetDistance" : 25.4 * mm});
        }
        {
            var Q0;
            Q0=makeQuery(id+"F11.imprint","IMPRINT",FACE,{"disambiguationData":[TD([[makeQuery(id+"F11.imprint","IMPRINT",EDGE,{"derivedFrom":sQuery(id+"F11.wireOp",EDGE,"E89")}),1.0]])]});
            var Q1;
            Q1=makeQuery(id+"F11.imprint","IMPRINT",FACE,{"disambiguationData":[TD([[makeQuery(id+"F11.imprint","IMPRINT",EDGE,{"derivedFrom":sQuery(id+"F11.wireOp",EDGE,"E92")}),-1.0]])]});
            extrude(context, id + "F16", {"entities" : qUnion([Q0, Q1]), "depth" : 152.4 * mm, "offsetDistance" : 25.4 * mm});
        }
        {
            var Q0;
            Q0=makeQuery(id+"F8.opExtrude","CAP_FACE",FACE,{"disambiguationData":[OSD([sQuery(id+"F7.wireOp",EDGE,"E66.0"),sQuery(id+"F7.wireOp",EDGE,"E66.3"),sQuery(id+"F7.wireOp",EDGE,"E67.0"),sQuery(id+"F7.wireOp",EDGE,"E67.1"),sQuery(id+"F7.wireOp",EDGE,"E67.2"),sQuery(id+"F7.wireOp",EDGE,"E67.4"),sQuery(id+"F7.wireOp",EDGE,"E67.5"),sQuery(id+"F7.wireOp",EDGE,"E67.6"),sQuery(id+"F7.wireOp",EDGE,"E68"),sQuery(id+"F7.wireOp",EDGE,"E69"),sQuery(id+"F7.wireOp",EDGE,"E71"),sQuery(id+"F7.wireOp",EDGE,"E72.MirrorCS"),sQuery(id+"F7.wireOp",EDGE,"E73"),sQuery(id+"F7.wireOp",EDGE,"E74"),sQuery(id+"F7.wireOp",EDGE,"E75"),sQuery(id+"F7.wireOp",EDGE,"E76"),sQuery(id+"F7.wireOp",EDGE,"E77"),sQuery(id+"F7.wireOp",EDGE,"E78"),sQuery(id+"F7.wireOp",EDGE,"E80"),sQuery(id+"F7.wireOp",EDGE,"E81")])],"isStart":false});
            cPlane(context, id + "F17", {"entities" : qUnion([Q0]), "cplaneType" : CPlaneType.OFFSET, "offset" : 0 * mm, "width" : 152.4 * mm, "height" : 152.4 * mm});
        }
        {
            var Q0;
            Q0=qCreatedBy(id+"F17.planeOp",FACE);
            var sketch = newSketch(context, id + "F18", { "sketchPlane" : qUnion([Q0])});
            skPoint(sketch, "E108.0", {"position": v(-660.4, -1219.2) * mm});
            skPoint(sketch, "E108.1", {"position": v(-660.4, 1219.2) * mm});
            skPoint(sketch, "E108.2", {"position": v(660.4, 1219.2) * mm});
            skPoint(sketch, "E108.3", {"position": v(660.4, -1219.2) * mm});
            skLineSegment(sketch, "E109", {"start": v(-660.4, 1219.2) * mm, "end": v(-660.4, -1219.2) * mm, "construction": true});
            skLineSegment(sketch, "E110", {"start": v(660.4, -1219.2) * mm, "end": v(660.4, 1219.2) * mm, "construction": true});
            skSolve(sketch);
        }
        {
            var Q0;
            Q0=makeQuery(id+"F15.opExtrude","SWEPT_FACE",FACE,{"disambiguationData":[OSD([sQuery(id+"F13.wireOp",EDGE,"E103")])]});
            cPlane(context, id + "F19", {"entities" : qUnion([Q0]), "cplaneType" : CPlaneType.OFFSET, "offset" : 0 * mm, "width" : 152.4 * mm, "height" : 152.4 * mm});
        }
        {
            var Q0;
            Q0=qCreatedBy(id+"F19.planeOp",FACE);
            var sketch = newSketch(context, id + "F20", { "sketchPlane" : qUnion([Q0])});
            skLineSegment(sketch, "E111.0", {"start": v(203.09, 50.8) * mm, "end": v(203.09, -266.7) * mm});
            skLineSegment(sketch, "E111.1", {"start": v(203.09, -419.1) * mm, "end": v(203.09, -495.3) * mm});
            skLineSegment(sketch, "E111.2", {"start": v(203.09, -647.7) * mm, "end": v(203.09, -1219.2) * mm});
            skLineSegment(sketch, "E112", {"start": v(203.09, -457.2) * mm, "end": v(-559.34, -457.2) * mm});
            skLineSegment(sketch, "E113.0", {"start": v(-559.34, 1219.2) * mm, "end": v(-559.34, -1219.2) * mm, "construction": true});
            skLineSegment(sketch, "E114", {"start": v(-559.34, -1168.4) * mm, "end": v(203.09, -698.5) * mm});
            skLineSegment(sketch, "E115.0.3", {"start": v(-559.34, 304.8) * mm, "end": v(-660.03, 304.8) * mm});
            skPoint(sketch, "E116.orphan", {"position": v(-406.17, 304.8) * mm});
            skPoint(sketch, "E117.orphan", {"position": v(-230.17, 304.8) * mm});
            skPoint(sketch, "E118.orphan", {"position": v(-484.02, 304.8) * mm});
            skLineSegment(sketch, "E119", {"start": v(-559.34, -698.5) * mm, "end": v(203.09, -1168.4) * mm});
            skLineSegment(sketch, "E120", {"start": v(203.09, -203.2) * mm, "end": v(-559.34, -203.2) * mm});
            skSolve(sketch);
        }
        {
            var Q0;
            Q0=makeQuery(id+"F15.opExtrude","SWEPT_FACE",FACE,{"disambiguationData":[OSD([sQuery(id+"F13.wireOp",EDGE,"E106")])]});
            cPlane(context, id + "F21", {"entities" : qUnion([Q0]), "cplaneType" : CPlaneType.OFFSET, "offset" : 0 * mm, "width" : 152.4 * mm, "height" : 152.4 * mm});
        }
        {
            var Q0;
            Q0=qCreatedBy(id+"F21.planeOp",FACE);
            var sketch = newSketch(context, id + "F22", { "sketchPlane" : qUnion([Q0])});
            skLineSegment(sketch, "E121.0", {"start": v(-203.09, -647.7) * mm, "end": v(-203.09, -1219.2) * mm});
            skLineSegment(sketch, "E121.1", {"start": v(-203.09, -419.1) * mm, "end": v(-203.09, -495.3) * mm});
            skLineSegment(sketch, "E121.2", {"start": v(-203.09, 50.8) * mm, "end": v(-203.09, -266.7) * mm});
            skPoint(sketch, "E122.0", {"position": v(-203.09, -1168.4) * mm});
            skPoint(sketch, "E122.1", {"position": v(-203.09, -698.5) * mm});
            skPoint(sketch, "E122.2", {"position": v(-203.09, -457.2) * mm});
            skLineSegment(sketch, "E123", {"start": v(-203.09, -1168.4) * mm, "end": v(559.34, -698.5) * mm});
            skLineSegment(sketch, "E124.0", {"start": v(559.34, -1219.2) * mm, "end": v(559.34, 1219.2) * mm, "construction": true});
            skLineSegment(sketch, "E125", {"start": v(-203.09, -698.5) * mm, "end": v(559.34, -1168.4) * mm});
            skLineSegment(sketch, "E126", {"start": v(-203.09, -457.2) * mm, "end": v(559.34, -457.2) * mm});
            skLineSegment(sketch, "E127", {"start": v(-203.09, -203.2) * mm, "end": v(559.34, -203.2) * mm});
            skSolve(sketch);
        }
        {
            var Q0;
            Q0=makeQuery(id+"F16.opExtrude","SWEPT_FACE",FACE,{"disambiguationData":[OSD([sQuery(id+"F11.wireOp",EDGE,"E94")])]});
            cPlane(context, id + "F23", {"entities" : qUnion([Q0]), "cplaneType" : CPlaneType.OFFSET, "offset" : 0 * mm, "width" : 152.4 * mm, "height" : 152.4 * mm});
        }
        {
            var Q0;
            Q0=qCreatedBy(id+"F23.planeOp",FACE);
            var sketch = newSketch(context, id + "F24", { "sketchPlane" : qUnion([Q0])});
            skLineSegment(sketch, "E128.0", {"start": v(310.48, 1219.2) * mm, "end": v(310.48, 647.7) * mm});
            skLineSegment(sketch, "E128.1", {"start": v(310.48, 495.3) * mm, "end": v(310.48, 419.1) * mm});
            skLineSegment(sketch, "E128.2", {"start": v(310.48, 266.7) * mm, "end": v(310.48, -50.8) * mm});
            skLineSegment(sketch, "E129", {"start": v(310.48, 711.2) * mm, "end": v(-587.18, 1168.4) * mm});
            skLineSegment(sketch, "E130.0", {"start": v(-587.18, 1219.2) * mm, "end": v(-587.18, -1219.2) * mm, "construction": true});
            skLineSegment(sketch, "E131", {"start": v(310.48, 1168.4) * mm, "end": v(-587.18, 711.2) * mm});
            skLineSegment(sketch, "E132", {"start": v(310.48, 457.2) * mm, "end": v(-587.18, 457.2) * mm});
            skLineSegment(sketch, "E133", {"start": v(310.48, 203.2) * mm, "end": v(-587.18, 203.2) * mm});
            skSolve(sketch);
        }
        {
            var Q0;
            Q0=makeQuery(id+"F16.opExtrude","SWEPT_FACE",FACE,{"disambiguationData":[OSD([sQuery(id+"F11.wireOp",EDGE,"E91")])]});
            cPlane(context, id + "F25", {"entities" : qUnion([Q0]), "cplaneType" : CPlaneType.OFFSET, "offset" : 0 * mm, "width" : 152.4 * mm, "height" : 152.4 * mm});
        }
    });
